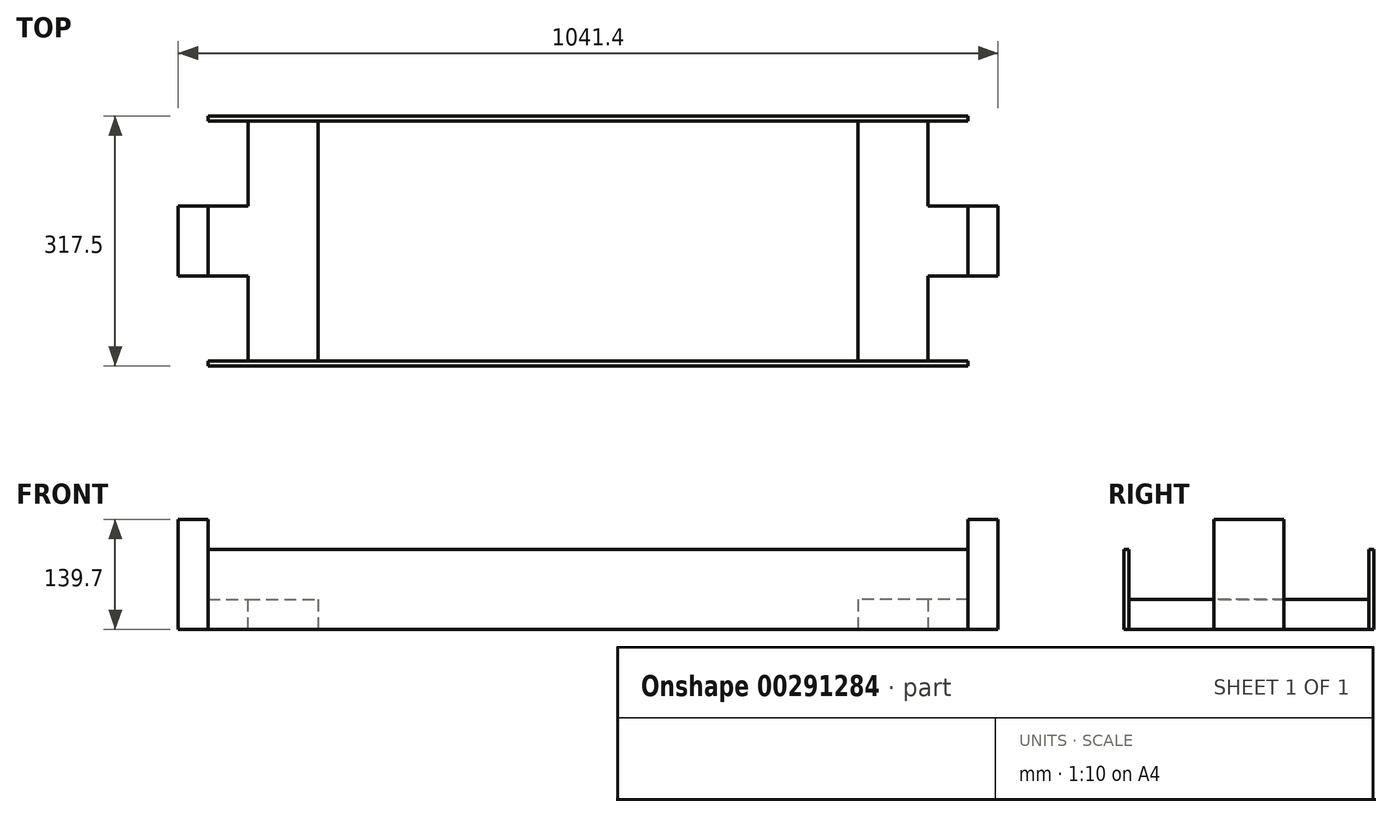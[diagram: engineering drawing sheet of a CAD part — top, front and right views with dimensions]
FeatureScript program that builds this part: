
annotation { "Feature Type Name" : "Feature", "Feature Type Description" : "" }
export const myFeature = defineFeature(function(context is Context, id is Id, definition is map)
    precondition{}
    {
        {
            var Q0;
            Q0=qCreatedBy(makeId("Front.planeOp"),FACE);
            var sketch = newSketch(context, id + "F0", { "sketchPlane" : qUnion([Q0])});
            skLineSegment(sketch, "E0", {"start": v(482.6, 50.8) * mm, "end": v(482.6, -50.8) * mm});
            skLineSegment(sketch, "E1", {"start": v(482.6, -50.8) * mm, "end": v(-482.6, -50.8) * mm});
            skLineSegment(sketch, "E2", {"start": v(-482.6, -50.8) * mm, "end": v(-482.6, 50.8) * mm});
            skLineSegment(sketch, "E3", {"start": v(-482.6, 50.8) * mm, "end": v(482.6, 50.8) * mm});
            skSolve(sketch);
        }
        {
            var Q0;
            Q0 = qSketchRegion(id + "F0", true);
            extrude(context, id + "F1", {"entities" : qUnion([Q0]), "depth" : 6.35 * mm});
        }
        {
            var Q0;
            Q0=makeQuery(id+"F1.opExtrude","CAP_FACE",FACE,{"disambiguationData":[OSD([sQuery(id+"F0.wireOp",EDGE,"E0"),sQuery(id+"F0.wireOp",EDGE,"E1"),sQuery(id+"F0.wireOp",EDGE,"E2"),sQuery(id+"F0.wireOp",EDGE,"E3")])],"isStart":false});
            var sketch = newSketch(context, id + "F2", { "sketchPlane" : qUnion([Q0])});
            skLineSegment(sketch, "E4", {"start": v(-431.8, -50.8) * mm, "end": v(-431.8, -12.7) * mm});
            skLineSegment(sketch, "E5", {"start": v(-431.8, -12.7) * mm, "end": v(-342.9, -12.7) * mm});
            skLineSegment(sketch, "E6", {"start": v(-342.9, -12.7) * mm, "end": v(-342.9, -50.8) * mm});
            skLineSegment(sketch, "E7", {"start": v(-342.9, -50.8) * mm, "end": v(-431.8, -50.8) * mm});
            skLineSegment(sketch, "E8.MirrorCS", {"start": v(431.8, -50.8) * mm, "end": v(431.8, -12.7) * mm});
            skLineSegment(sketch, "E9.MirrorCS", {"start": v(431.8, -12.7) * mm, "end": v(342.9, -12.7) * mm});
            skLineSegment(sketch, "E10.MirrorCS", {"start": v(342.9, -12.7) * mm, "end": v(342.9, -50.8) * mm});
            skLineSegment(sketch, "E11.MirrorCS", {"start": v(342.9, -50.8) * mm, "end": v(431.8, -50.8) * mm});
            skSolve(sketch);
        }
        {
            var Q0;
            Q0 = qSketchRegion(id + "F2", true);
            extrude(context, id + "F3", {"entities" : qUnion([Q0]), "operationType" : NewBodyOperationType.ADD, "depth" : 304.8 * mm});
        }
        {
            var Q0;
            Q0=makeQuery(id+"F3.opExtrude","SWEPT_FACE",FACE,{"disambiguationData":[OSD([sQuery(id+"F2.wireOp",EDGE,"E4")])]});
            var sketch = newSketch(context, id + "F4", { "sketchPlane" : qUnion([Q0])});
            skLineSegment(sketch, "E12", {"start": v(114.3, -50.8) * mm, "end": v(114.3, -12.7) * mm});
            skLineSegment(sketch, "E13", {"start": v(114.3, -12.7) * mm, "end": v(203.2, -12.7) * mm});
            skLineSegment(sketch, "E14", {"start": v(203.2, -12.7) * mm, "end": v(203.2, -50.8) * mm});
            skLineSegment(sketch, "E15", {"start": v(203.2, -50.8) * mm, "end": v(114.3, -50.8) * mm});
            skSolve(sketch);
        }
        {
            var Q0;
            Q0 = qSketchRegion(id + "F4", true);
            extrude(context, id + "F5", {"entities" : qUnion([Q0]), "operationType" : NewBodyOperationType.ADD, "depth" : 88.9 * mm});
        }
        {
            var Q0;
            Q0=makeQuery(id+"F5.boolean.opBoolean","MERGE",FACE,{"derivedFrom":[makeQuery(id+"F3.opExtrude","SWEPT_FACE",FACE,{"disambiguationData":[OSD([sQuery(id+"F2.wireOp",EDGE,"E5")])]}),makeQuery(id+"F5.opExtrude","SWEPT_FACE",FACE,{"disambiguationData":[OSD([sQuery(id+"F4.wireOp",EDGE,"E13")])]})]});
            var sketch = newSketch(context, id + "F6", { "sketchPlane" : qUnion([Q0])});
            skLineSegment(sketch, "E16", {"start": v(-520.7, -114.3) * mm, "end": v(-482.6, -114.3) * mm});
            skLineSegment(sketch, "E17", {"start": v(-482.6, -114.3) * mm, "end": v(-482.6, -203.2) * mm});
            skLineSegment(sketch, "E18", {"start": v(-482.6, -203.2) * mm, "end": v(-520.7, -203.2) * mm});
            skLineSegment(sketch, "E19", {"start": v(-520.7, -203.2) * mm, "end": v(-520.7, -114.3) * mm});
            skSolve(sketch);
        }
        {
            var Q0;
            Q0 = qSketchRegion(id + "F6", true);
            extrude(context, id + "F7", {"entities" : qUnion([Q0]), "operationType" : NewBodyOperationType.ADD, "depth" : 101.6 * mm});
        }
        {
            var Q0;
            Q0=makeQuery(id+"F3.opExtrude","SWEPT_FACE",FACE,{"disambiguationData":[OSD([sQuery(id+"F2.wireOp",EDGE,"E8.MirrorCS")])]});
            var sketch = newSketch(context, id + "F8", { "sketchPlane" : qUnion([Q0])});
            skLineSegment(sketch, "E20", {"start": v(-114.3, -50.8) * mm, "end": v(-114.3, -12.7) * mm});
            skPoint(sketch, "E20.endSnap0", {"position": v(-158.75, -12.7) * mm});
            skLineSegment(sketch, "E21", {"start": v(-114.3, -12.7) * mm, "end": v(-203.2, -12.7) * mm});
            skLineSegment(sketch, "E22", {"start": v(-203.2, -12.7) * mm, "end": v(-203.2, -50.8) * mm});
            skLineSegment(sketch, "E23", {"start": v(-203.2, -50.8) * mm, "end": v(-114.3, -50.8) * mm});
            skSolve(sketch);
        }
        {
            var Q0;
            Q0 = qSketchRegion(id + "F8", true);
            extrude(context, id + "F9", {"entities" : qUnion([Q0]), "operationType" : NewBodyOperationType.ADD, "depth" : 88.9 * mm});
        }
        {
            var Q0;
            Q0=makeQuery(id+"F9.boolean.opBoolean","MERGE",FACE,{"derivedFrom":[makeQuery(id+"F3.opExtrude","SWEPT_FACE",FACE,{"disambiguationData":[OSD([sQuery(id+"F2.wireOp",EDGE,"E9.MirrorCS")])]}),makeQuery(id+"F9.opExtrude","SWEPT_FACE",FACE,{"disambiguationData":[OSD([sQuery(id+"F8.wireOp",EDGE,"E21")])]})]});
            var sketch = newSketch(context, id + "F10", { "sketchPlane" : qUnion([Q0])});
            skLineSegment(sketch, "E24", {"start": v(520.7, -203.2) * mm, "end": v(482.6, -203.2) * mm});
            skLineSegment(sketch, "E25", {"start": v(482.6, -203.2) * mm, "end": v(482.6, -114.3) * mm});
            skLineSegment(sketch, "E26", {"start": v(482.6, -114.3) * mm, "end": v(520.7, -114.3) * mm});
            skLineSegment(sketch, "E27", {"start": v(520.7, -114.3) * mm, "end": v(520.7, -203.2) * mm});
            skSolve(sketch);
        }
        {
            var Q0;
            Q0 = qSketchRegion(id + "F10", true);
            extrude(context, id + "F11", {"entities" : qUnion([Q0]), "operationType" : NewBodyOperationType.ADD, "depth" : 101.6 * mm});
        }
        {
            var Q0;
            Q0=makeQuery(id+"F3.opExtrude","CAP_FACE",FACE,{"disambiguationData":[OSD([sQuery(id+"F2.wireOp",EDGE,"E4"),sQuery(id+"F2.wireOp",EDGE,"E5"),sQuery(id+"F2.wireOp",EDGE,"E6"),sQuery(id+"F2.wireOp",EDGE,"E7")])],"isStart":false});
            var sketch = newSketch(context, id + "F12", { "sketchPlane" : qUnion([Q0])});
            skLineSegment(sketch, "E28", {"start": v(-431.8, -50.8) * mm, "end": v(-482.6, -50.8) * mm});
            skLineSegment(sketch, "E29", {"start": v(-482.6, -50.8) * mm, "end": v(-482.6, 50.8) * mm});
            skLineSegment(sketch, "E30", {"start": v(-482.6, 50.8) * mm, "end": v(482.6, 50.8) * mm});
            skLineSegment(sketch, "E31", {"start": v(482.6, 50.8) * mm, "end": v(482.6, -50.8) * mm});
            skLineSegment(sketch, "E32", {"start": v(482.6, -50.8) * mm, "end": v(-482.6, -50.8) * mm});
            skSolve(sketch);
        }
        {
            var Q0;
            Q0 = qSketchRegion(id + "F12", true);
            extrude(context, id + "F13", {"entities" : qUnion([Q0]), "operationType" : NewBodyOperationType.ADD, "depth" : 6.35 * mm});
        }
    });
